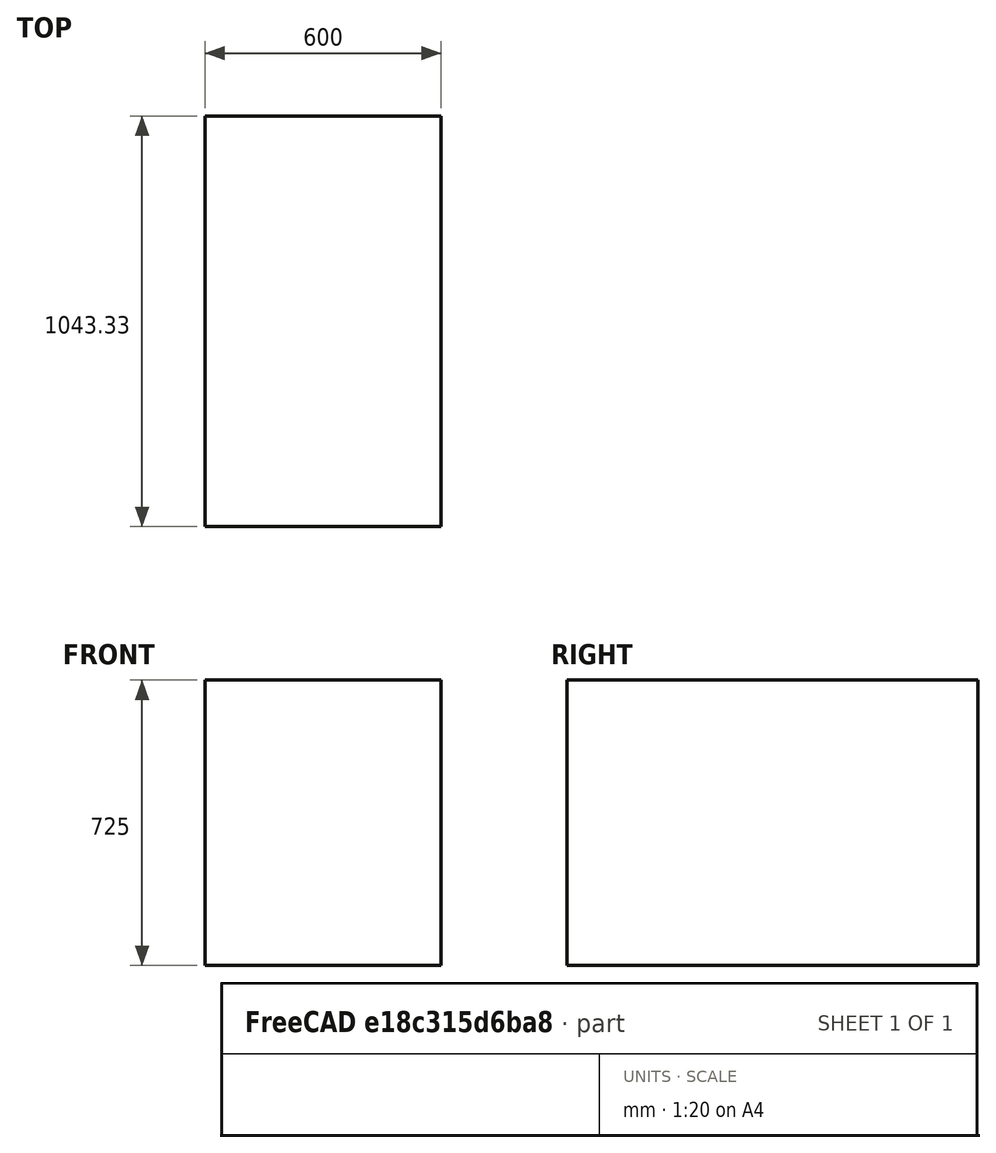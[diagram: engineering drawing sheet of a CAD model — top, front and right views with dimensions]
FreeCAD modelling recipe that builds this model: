
FCSTD DOCUMENT  (FreeCAD 0.19R24291 (Git))
Label: leftBuiltIn2
License: All rights reserved
LicenseURL: http://en.wikipedia.org/wiki/All_rights_reserved
objects: Sketcher::SketchObject×1, PartDesign::Pad×1, PartDesign::Body×1
note: 4 computed .brp shape members not serialized (recipe doc carries the construction recipe); baked Part::Feature solids carry a one-line shape summary decoded from their .brp

FEATURE [Sketcher::SketchObject] Sketch
  FullyConstrained = false
  MapMode = 5
  Placement = pos=(0,0,0) rot=(0.57735,0.57735,0.57735;2.0944rad)
  Support = -> [YZ_Plane]
  expr: Constraints[8] = 3130 / 3
  sketch-geometry (8):
    g0: LineSegment StartX=-1043.33 StartY=725 StartZ=0 EndX=0 EndY=725 EndZ=0
    g1: LineSegment StartX=0 StartY=725 StartZ=0 EndX=0 EndY=0 EndZ=0
    g2: LineSegment StartX=0 StartY=0 StartZ=0 EndX=-1043.33 EndY=0 EndZ=0
    g3: LineSegment StartX=-1043.33 StartY=0 StartZ=0 EndX=-1043.33 EndY=725 EndZ=0
    g4: LineSegment StartX=-3667.4 StartY=1853.05 StartZ=0 EndX=-537.403 EndY=1853.05 EndZ=0
    g5: LineSegment StartX=-537.403 StartY=1853.05 StartZ=0 EndX=-537.403 EndY=1128.05 EndZ=0
    g6: LineSegment StartX=-537.403 StartY=1128.05 StartZ=0 EndX=-3667.4 EndY=1128.05 EndZ=0
    g7: LineSegment StartX=-3667.4 StartY=1128.05 StartZ=0 EndX=-3667.4 EndY=1853.05 EndZ=0
  constraints (21):
    c: Coincident(g0,g1)
    c: Coincident(g1,g2)
    c: Coincident(g2,g3)
    c: Coincident(g3,g0)
    c: Horizontal(g0)
    c: Horizontal(g2)
    c: Vertical(g1)
    c: Vertical(g3)
    c: DistanceX(g2,g2) = 1043.33
    c: DistanceY(g3,g3) = 725
    c: Coincident(g4,g5)
    c: Coincident(g5,g6)
    c: Coincident(g6,g7)
    c: Coincident(g7,g4)
    c: Horizontal(g4)
    c: Horizontal(g6)
    c: Vertical(g5)
    c: Vertical(g7)
    c: DistanceY(g7,g7) = 725
    c: DistanceX(g6,g6) = 3130
    c: Coincident(g1,g-1)
FEATURE [PartDesign::Pad] Pad
  Direction = (1,1,1)
  Length = 600
  Length2 = 100
  Placement = pos=(0,0,0) rot=(0.57735,0.57735,0.57735;2.0944rad)
  Profile = -> Sketch
  Type = 0
FEATURE [PartDesign::Body] Body
  Group = -> [Sketch,Pad]
  Origin = -> Origin
  Tip = -> Pad
